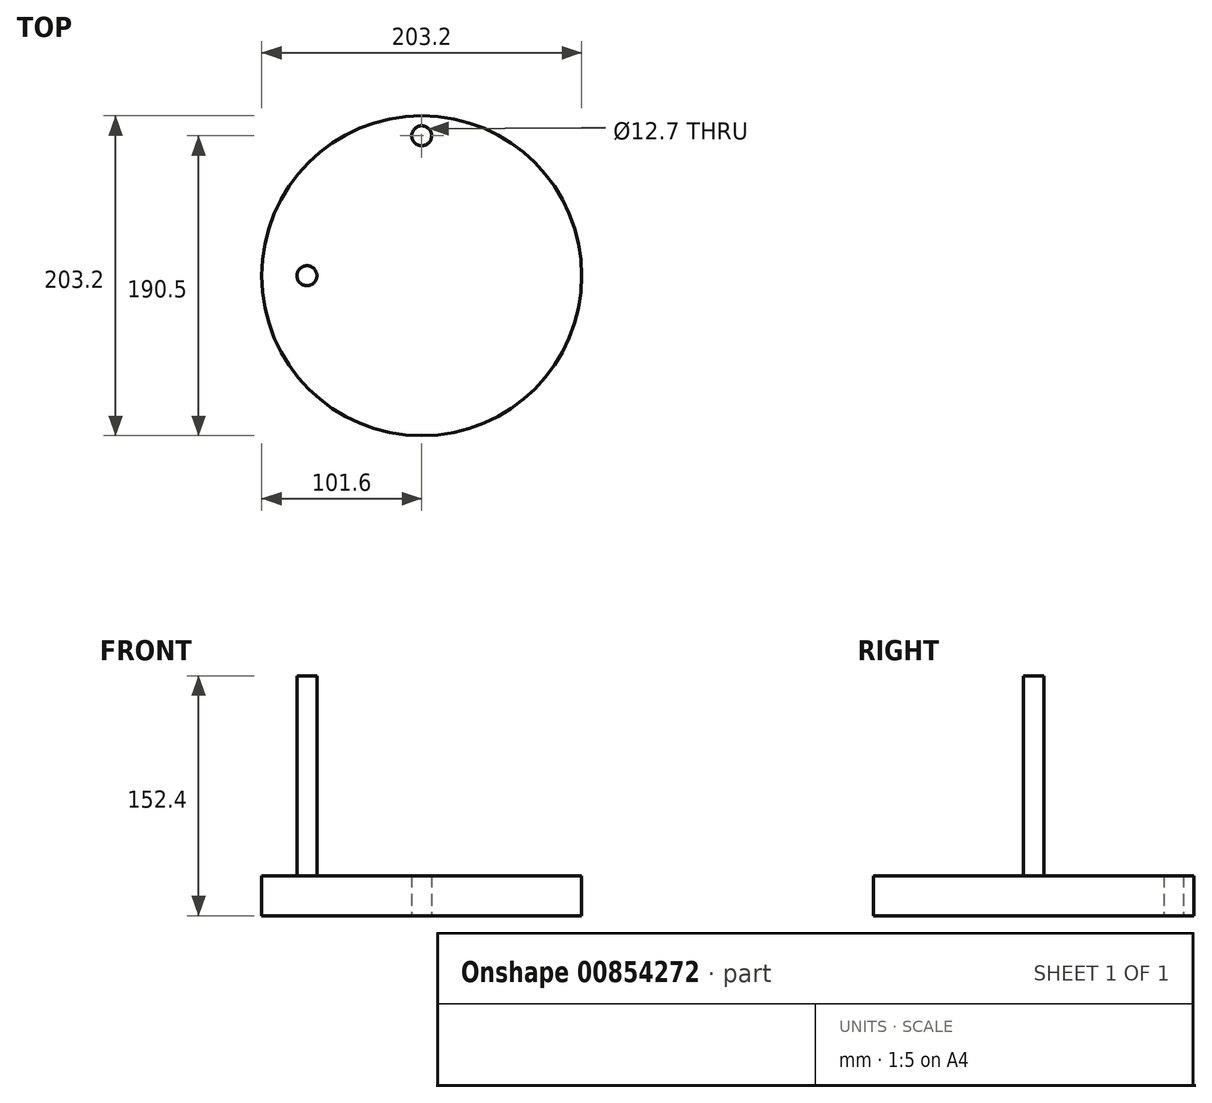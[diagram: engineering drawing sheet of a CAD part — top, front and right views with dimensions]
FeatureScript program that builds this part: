
annotation { "Feature Type Name" : "Feature", "Feature Type Description" : "" }
export const myFeature = defineFeature(function(context is Context, id is Id, definition is map)
    precondition{}
    {
        {
            var Q0;
            Q0=qCreatedBy(makeId("Top.planeOp"),FACE);
            var sketch = newSketch(context, id + "F0", { "sketchPlane" : qUnion([Q0])});
            skCircle(sketch, "E0", {"center": v(0, 0) * mm, "radius": 101.6 * mm});
            skSolve(sketch);
        }
        {
            var Q0;
            Q0=qSketchRegion(id+"F0",true);
            extrude(context, id + "F1", {"entities" : qUnion([Q0]), "depth" : 25.4 * mm, "offsetDistance" : 25.4 * mm});
        }
        {
            var Q0;
            Q0=makeQuery(id+"F1.opExtrude","CAP_FACE",FACE,{"disambiguationData":[OSD([sQuery(id+"F0.wireOp",EDGE,"E0")])],"isStart":true});
            var sketch = newSketch(context, id + "F2", { "sketchPlane" : qUnion([Q0])});
            skPoint(sketch, "E1", {"position": v(0, -88.9) * mm});
            skSolve(sketch);
        }
        {
            var Q0;
            Q0=sQuery(id+"F2.wireOp",VERTEX,"E1");
            var Q1;
            Q1=makeQuery(id+"F1.opExtrude","SWEPT_BODY",BODY,{"disambiguationData":[OSD([sQuery(id+"F0.wireOp",EDGE,"E0")])]});
            hole(context, id + "F3", {"style" : HoleStyle.SIMPLE, "endStyle" : HoleEndStyle.THROUGH, "holeDiameter" : 12.7 * mm, "majorDiameter" : 6.35 * mm, "isTappedThrough" : true, "tappedDepth" : 12.7 * mm, "tapClearance" : 3, "locations" : qUnion([Q0]), "scope" : qUnion([Q1])});
        }
        {
            var Q0;
            Q0=makeQuery(id+"F1.opExtrude","CAP_FACE",FACE,{"disambiguationData":[OSD([sQuery(id+"F0.wireOp",EDGE,"E0")])],"isStart":false});
            var sketch = newSketch(context, id + "F4", { "sketchPlane" : qUnion([Q0])});
            skCircle(sketch, "E2", {"center": v(-72.82, 0) * mm, "radius": 6.35 * mm});
            skSolve(sketch);
        }
        {
            var Q0;
            Q0=makeQuery(id+"F4.imprint","IMPRINT",FACE,{"disambiguationData":[TD([[makeQuery(id+"F4.imprint","IMPRINT",EDGE,{"derivedFrom":sQuery(id+"F4.wireOp",EDGE,"E2")}),1.0]])]});
            var Q1;
            Q1=sQuery(id+"F4.wireOp",EDGE,"E2");
            extrude(context, id + "F5", {"entities" : qUnion([Q0]), "operationType" : NewBodyOperationType.ADD, "surfaceEntities" : qUnion([Q1]), "depth" : 127 * mm, "offsetDistance" : 25.4 * mm});
        }
    });
